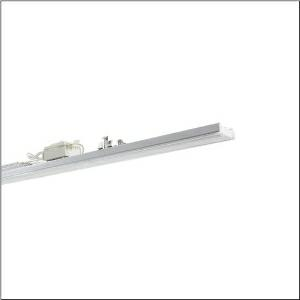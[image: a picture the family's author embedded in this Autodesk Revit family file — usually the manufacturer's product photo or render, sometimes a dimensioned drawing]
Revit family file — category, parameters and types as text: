
# Revit family: licross_r__11_recessed_mo_51te19cn485g_e7a3
name_source: partatom
category: Lighting Fixtures
units: mm (PartAtom-declared; Revit-internal decimal feet)

## family parameters
Cut with Voids When Loaded = No
Host = Face
Light Source = No
Part Type = Normal
Room Calculation Point = No
Round Connector Dimension = Use Diameter
Shared = No

## types (1)
- --- (1 x LED, 8920 lm, 49.3 W, 4000K)
    Apparent Load = 49 VA
    CIE Flux Codes = 55 90 98 100 100
    Color Rendering = 80
    Color Temperature = 4000K
    Default Elevation = 1800 mm
    Description = Licross® 11 Recessed MO, luminaire insert, of sheet steel, galvanised, coil coated, white, length: 1.500mm, width: 66mm, height: 67mm, LED rated luminous flux: 8.920lm, light colour: 840, control gear: ON/OFF Multilumen, CLOi, with plug, 3-pole, with phase selection, mains connection: 220..240V, AC, 50/60Hz, start of lifetime: 49W, end of service life: 55W, internal wiring halogen-free, primary light control with lens, of plastic, primary optical cover: cover, of PMMA, light emission: direct distribution, primary light characteristic: double asymmetric, protection rating (complete): IP54, insulation class (complete): insulation class I (protective earthing), certification: CE, ENEC, VDE, UKCA, protection symbol: D if used in an environment with non-conductive dust loads with corresponding accessories, impact resistance: IK06, permissible ambient temperature for indoor applications: -35..+40°C, corresponds to IFS (International Featured Standards) requirements for safety and quality in the food industry, reducing of maximum allowable ambient temperature of 5°C with ceiling mounting, LABS conformity tested according to VDMA 24364:2018-05, packaging unit: 1 piece
    Height = 58 mm
    Lamp = 1 x LED
    Lamp Light Flux = 8920 lm
    Lamp Power = 49.3 W
    Lamp count = 1
    Length = 1500 mm
    Luminous efficacy = 181 lm/W
    Manufacturer = Siteco
    ModVariant = No
    Model = 51TE19CN485G
    Mounting Place = Ceiling
    Mounting Type = Pendant
    Number of Poles = 1
    OnlyDefault = Yes
    Power Factor = 1
    Product Name = Licross® 11 Recessed MO
    Product group = luminaire insert | ceiling pendant
    ProductGroupID = 902
    Protection Class = Protection class I
    Protection Degree = IP 54
    RLX_Detail_Level = 1
    RLX_Emergency_Light_Flux = 0 lm
    RLX_Emergency_Type = 0
    RLX_Emergency_Type_DB = No
    RlxData = <blob elided: 22389 chars, md5=841acc0f>
    Socket = socket
    Standby Power = 0 W
    System Light Flux = 8920 lm
    System Power = 49 W
    Type Comments = factory setting: luminous flux: 100 % | (A | C | E) | 113 mA
    Type Image = l_1296930.jpg
    URL = http://relux.com
    VarID = @adj_107125
    Voltage = 0 V
    Weight = 0.00 kg
    Width = 66 mm

## geometry (parser evidence)
native form markers: Blend x4, Sweep x11
no freeform markers — native parametric forms only
